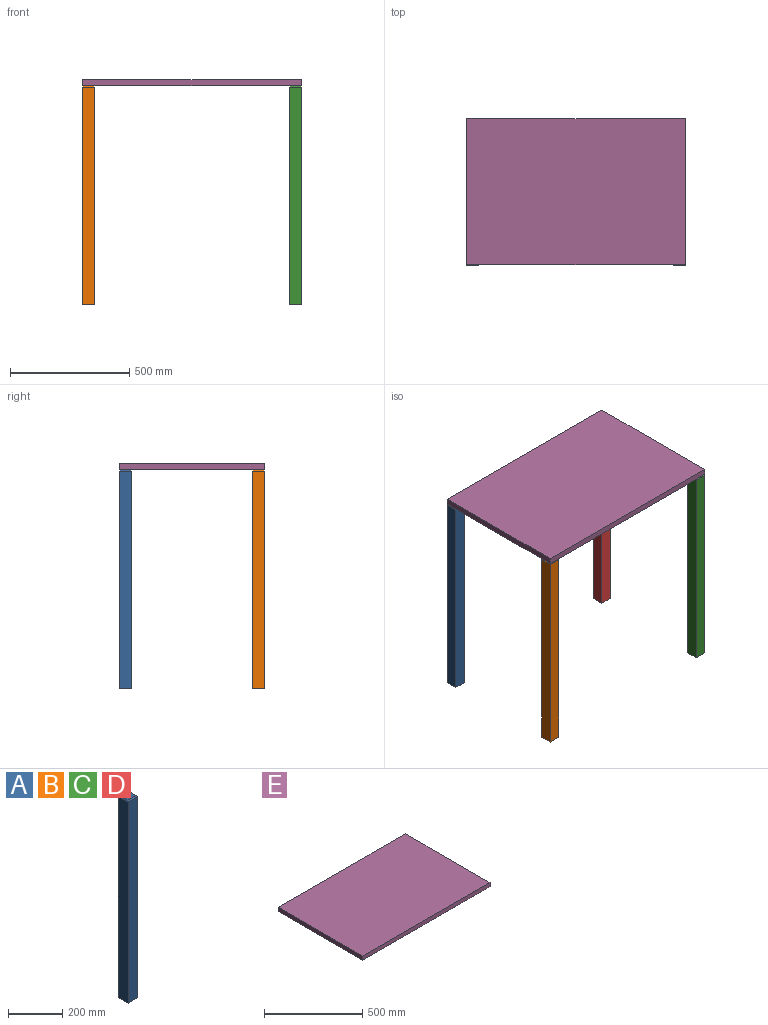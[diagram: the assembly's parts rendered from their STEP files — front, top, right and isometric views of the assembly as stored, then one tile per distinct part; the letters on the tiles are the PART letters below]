
ASSEMBLY  parts=5 mates=14
PART A: 10 faces, bbox 50.8x50.8x914.4 mm
  f0: plane 909.32x50.8mm, normal (-1,0,0), area 46193.5mm2, adj f1,f4,f5,f7
  f1: plane 50.8x50.8mm, normal (0,0,-1), area 2580.6mm2, adj f0,f2,f4,f5
  f2: plane 909.32x50.8mm, normal (1,0,0), area 46193.5mm2, adj f1,f4,f5,f8
  f3: plane 40.64x40.64mm, normal (0,0,1), area 1651.6mm2, adj f6,f7,f8,f9
  f4: plane 909.32x50.8mm, normal (0,-1,0), area 46193.5mm2, adj f0,f1,f2,f9
  f5: plane 909.32x50.8mm, normal (0,1,0), area 46193.5mm2, adj f0,f1,f2,f6
  f6: plane 50.8x5.08mm, normal (0,0.71,0.71), area 328.5mm2, adj f3,f5,f7,f8
  f7: plane 50.8x5.08mm, normal (-0.71,0,0.71), area 328.5mm2, adj f0,f3,f6,f9
  f8: plane 50.8x5.08mm, normal (0.71,0,0.71), area 328.5mm2, adj f2,f3,f6,f9
  f9: plane 50.8x5.08mm, normal (0,-0.71,0.71), area 328.5mm2, adj f3,f4,f7,f8
PART B: same geometry as A
PART C: same geometry as A
PART D: same geometry as A
PART E: 6 faces, bbox 914.4x609.6x25.4 mm
  f0: plane 609.6x25.4mm, normal (1,0,0), area 15483.8mm2, adj f1,f3,f4,f5
  f1: plane 914.4x25.4mm, normal (0,1,0), area 23225.8mm2, adj f0,f2,f4,f5
  f2: plane 609.6x25.4mm, normal (-1,0,0), area 15483.8mm2, adj f1,f3,f4,f5
  f3: plane 914.4x25.4mm, normal (0,-1,0), area 23225.8mm2, adj f0,f2,f4,f5
  f4: plane 914.4x609.6mm, normal (0,0,1), area 557418.2mm2, adj f0,f1,f2,f3
  f5: plane 914.4x609.6mm, normal (0,0,-1), area 557418.2mm2, adj f0,f1,f2,f3
PLACE A t=(-320.38,365.92,-35.83)mm
PLACE B t=(-320.38,-192.88,-35.83)mm fixed
PLACE C t=(543.22,-192.88,-35.83)mm
PLACE D t=(543.22,365.92,-35.83)mm
PLACE E t=(136.82,61.12,878.57)mm
MATE planar C.f4 <-> E.f3  axis (0,-1,0) through (568.62,-243.68,418.83)mm
MATE planar D.f3 <-> C.f3  axis (0,0,1) through (568.62,340.52,878.57)mm
MATE planar B.f3 <-> E.f5  axis (0,0,1) through (-294.98,-218.28,878.57)mm
MATE planar C.f2 <-> E.f0  axis (1,0,0) through (594.02,-218.28,418.83)mm
MATE planar D.f3 <-> B.f3  axis (0,0,1) through (568.62,340.52,878.57)mm
MATE planar B.f0 <-> E.f2  axis (-1,0,0) through (-320.38,-218.28,418.83)mm
MATE planar A.f0 <-> E.f2  axis (-1,0,0) through (-320.38,340.52,418.83)mm
MATE planar C.f3 <-> B.f3  axis (0,0,1) through (568.62,-218.28,878.57)mm
MATE parallel B.f0 <-> E.f2  axis (-1,0,0) through (-320.38,-218.28,418.83)mm
MATE planar A.f3 <-> B.f3  axis (0,0,1) through (-294.98,340.52,878.57)mm
MATE planar D.f5 <-> E.f1  axis (0,1,0) through (568.62,365.92,418.83)mm
MATE planar A.f5 <-> E.f1  axis (0,1,0) through (-294.98,365.92,418.83)mm
MATE planar B.f4 <-> E.f3  axis (0,-1,0) through (-294.98,-243.68,418.83)mm
MATE planar D.f2 <-> E.f0  axis (1,0,0) through (594.02,340.52,418.83)mm
